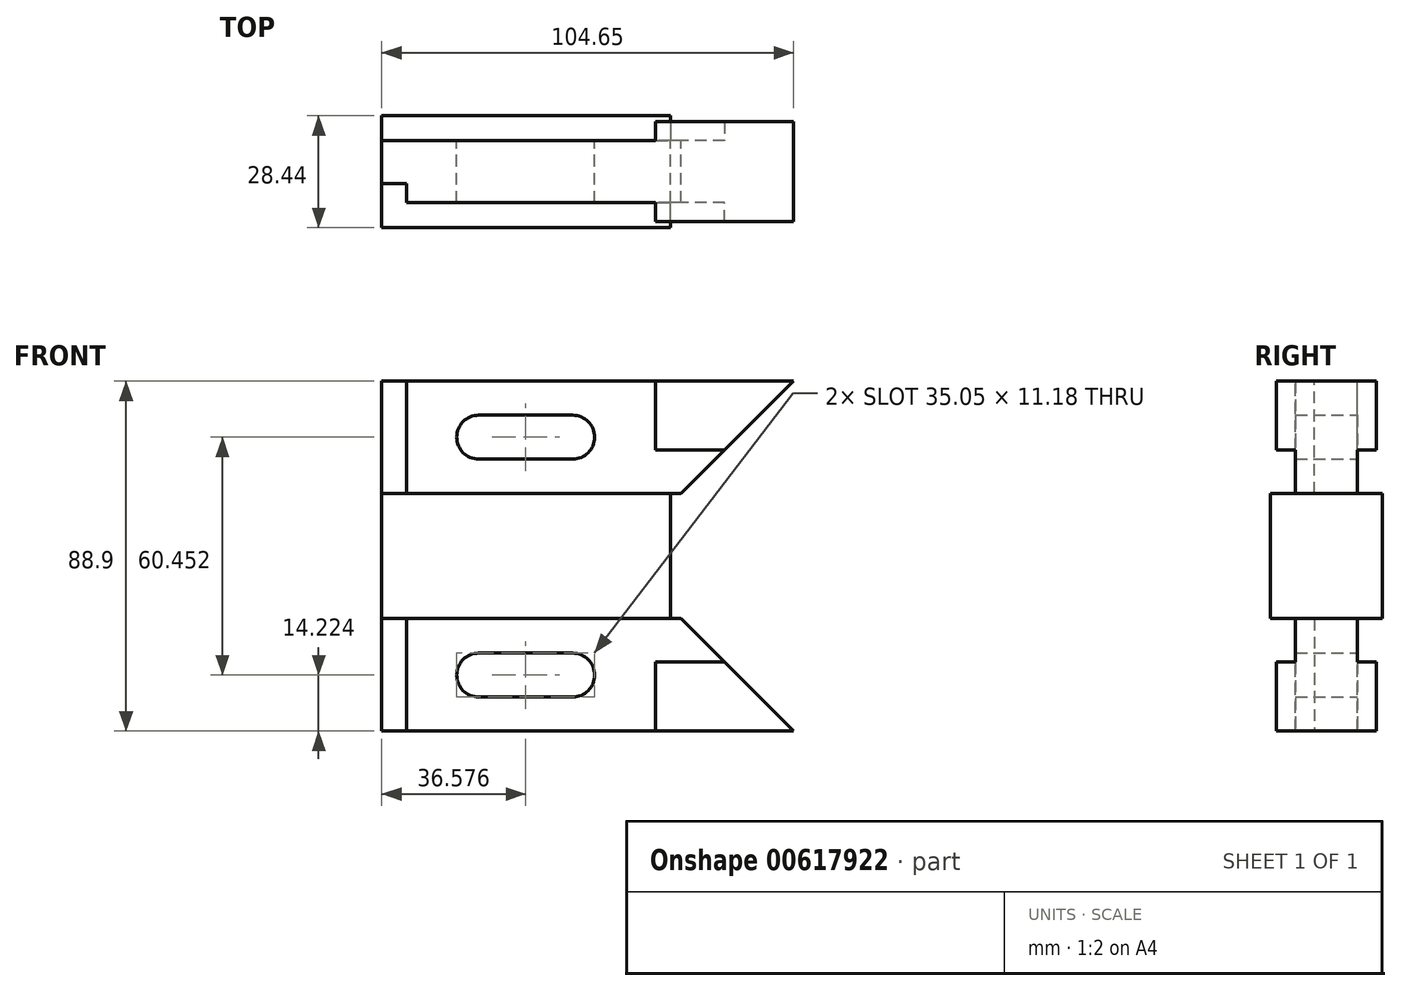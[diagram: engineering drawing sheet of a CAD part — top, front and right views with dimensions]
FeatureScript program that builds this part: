
annotation { "Feature Type Name" : "Feature", "Feature Type Description" : "" }
export const myFeature = defineFeature(function(context is Context, id is Id, definition is map)
    precondition{}
    {
        {
            var Q0;
            Q0=qCreatedBy(makeId("Front.planeOp"),FACE);
            var sketch = newSketch(context, id + "F0", { "sketchPlane" : qUnion([Q0])});
            skLineSegment(sketch, "E0", {"start": v(0, 0) * mm, "end": v(0, 44.45) * mm});
            skLineSegment(sketch, "E1", {"start": v(0, 44.45) * mm, "end": v(104.65, 44.45) * mm});
            skLineSegment(sketch, "E2", {"start": v(104.65, 44.45) * mm, "end": v(76.07, 15.88) * mm});
            skLineSegment(sketch, "E3", {"start": v(76.07, 15.88) * mm, "end": v(0, 15.88) * mm});
            skLineSegment(sketch, "E4", {"start": v(0, 0) * mm, "end": v(94.14, 0) * mm});
            skArc(sketch, "E5", {"start": v(24.64, 35.81) * mm, "mid": v(19.05, 30.23) * mm, "end": v(24.64, 24.64) * mm});
            skArc(sketch, "E6", {"start": v(48.51, 24.64) * mm, "mid": v(54.1, 30.23) * mm, "end": v(48.51, 35.81) * mm});
            skLineSegment(sketch, "E7", {"start": v(24.64, 35.81) * mm, "end": v(48.51, 35.81) * mm});
            skLineSegment(sketch, "E8", {"start": v(24.64, 24.64) * mm, "end": v(48.51, 24.64) * mm});
            skLineSegment(sketch, "E9", {"start": v(69.6, 44.45) * mm, "end": v(69.6, 26.92) * mm});
            skLineSegment(sketch, "E10", {"start": v(69.6, 26.92) * mm, "end": v(87.12, 26.92) * mm});
            skLineSegment(sketch, "E11", {"start": v(6.35, 44.45) * mm, "end": v(6.35, 15.88) * mm});
            skLineSegment(sketch, "E12", {"start": v(24.64, 30.23) * mm, "end": v(48.51, 30.23) * mm, "construction": true});
            skLineSegment(sketch, "E13", {"start": v(-38.06, 0) * mm, "end": v(126.35, 0) * mm, "construction": true});
            skLineSegment(sketch, "E14.MirrorCS", {"start": v(6.35, -44.45) * mm, "end": v(6.35, -15.88) * mm});
            skArc(sketch, "E15.MirrorCS", {"start": v(48.51, -24.64) * mm, "mid": v(54.1, -30.23) * mm, "end": v(48.51, -35.81) * mm});
            skLineSegment(sketch, "E16.MirrorCS", {"start": v(69.6, -26.92) * mm, "end": v(87.12, -26.92) * mm});
            skLineSegment(sketch, "E17.MirrorCS", {"start": v(104.65, -44.45) * mm, "end": v(76.07, -15.88) * mm});
            skArc(sketch, "E18.MirrorCS", {"start": v(24.64, -35.81) * mm, "mid": v(19.05, -30.23) * mm, "end": v(24.64, -24.64) * mm});
            skLineSegment(sketch, "E19.MirrorCS", {"start": v(0, -44.45) * mm, "end": v(104.65, -44.45) * mm});
            skLineSegment(sketch, "E20.MirrorCS", {"start": v(24.64, -24.64) * mm, "end": v(48.51, -24.64) * mm});
            skLineSegment(sketch, "E21.MirrorCS", {"start": v(24.64, -35.81) * mm, "end": v(48.51, -35.81) * mm});
            skLineSegment(sketch, "E22.MirrorCS", {"start": v(24.64, -30.23) * mm, "end": v(48.51, -30.23) * mm, "construction": true});
            skLineSegment(sketch, "E23.MirrorCS", {"start": v(69.6, -44.45) * mm, "end": v(69.6, -26.92) * mm});
            skLineSegment(sketch, "E24.MirrorCS", {"start": v(76.07, -15.88) * mm, "end": v(0, -15.88) * mm});
            skLineSegment(sketch, "E25.MirrorCS", {"start": v(0, 0) * mm, "end": v(0, -44.45) * mm});
            skLineSegment(sketch, "E26", {"start": v(73.4, -15.87) * mm, "end": v(73.4, 15.87) * mm});
            skSolve(sketch);
        }
        {
            var Q0;
            Q0=qSketchRegion(id+"F0",true);
            extrude(context, id + "F1", {"entities" : qUnion([Q0]), "depth" : 7.87 * mm});
        }
        {
            var Q0;
            {var subQ0=sQuery(id+"F0.wireOp",EDGE,"E4");Q0=makeQuery(id+"F0.imprint","IMPRINT",FACE,{"disambiguationData":[TD([[makeQuery(id+"F0.imprint","IMPRINT",EDGE,{"derivedFrom":subQ0}),1.0]])]});}
            var Q1;
            {var subQ1=sQuery(id+"F0.wireOp",EDGE,"E4");Q1=makeQuery(id+"F0.imprint","IMPRINT",FACE,{"disambiguationData":[TD([[makeQuery(id+"F0.imprint","IMPRINT",EDGE,{"derivedFrom":subQ1}),-1.0]])]});}
            extrude(context, id + "F2", {"entities" : qUnion([Q0, Q1]), "operationType" : NewBodyOperationType.ADD, "depth" : 14.22 * mm});
        }
        {
            var Q0;
            {var subQ3=sQuery(id+"F0.wireOp",EDGE,"E9");Q0=makeQuery(id+"F0.imprint","IMPRINT",FACE,{"disambiguationData":[TD([[makeQuery(id+"F0.imprint","IMPRINT",EDGE,{"derivedFrom":subQ3}),1.0]])]});}
            var Q1;
            {var subQ0=sQuery(id+"F0.wireOp",EDGE,"E16.MirrorCS");Q1=makeQuery(id+"F0.imprint","IMPRINT",FACE,{"disambiguationData":[TD([[makeQuery(id+"F0.imprint","IMPRINT",EDGE,{"derivedFrom":subQ0}),-1.0]])]});}
            extrude(context, id + "F3", {"entities" : qUnion([Q0, Q1]), "operationType" : NewBodyOperationType.ADD, "depth" : 12.7 * mm});
        }
        {
            var Q0;
            Q0=makeQuery(id+"F1.opExtrude","SWEPT_BODY",BODY,{"disambiguationData":[OSD([sQuery(id+"F0.wireOp",EDGE,"E0"),sQuery(id+"F0.wireOp",EDGE,"E1"),sQuery(id+"F0.wireOp",EDGE,"E2"),sQuery(id+"F0.wireOp",EDGE,"dfV1hQ6U-fgLX-1oEq-Cl2Z-QLcZu5KokJ9a"),sQuery(id+"F0.wireOp",EDGE,"E5"),sQuery(id+"F0.wireOp",EDGE,"E6"),sQuery(id+"F0.wireOp",EDGE,"E7"),sQuery(id+"F0.wireOp",EDGE,"E8"),sQuery(id+"F0.wireOp",EDGE,"E15.MirrorCS"),sQuery(id+"F0.wireOp",EDGE,"E17.MirrorCS"),sQuery(id+"F0.wireOp",EDGE,"E18.MirrorCS"),sQuery(id+"F0.wireOp",EDGE,"E19.MirrorCS"),sQuery(id+"F0.wireOp",EDGE,"E20.MirrorCS"),sQuery(id+"F0.wireOp",EDGE,"E21.MirrorCS"),sQuery(id+"F0.wireOp",EDGE,"E25.MirrorCS"),sQuery(id+"F0.wireOp",EDGE,"4e4c7bbf-45cc-40e8-b10d-9f1884ca9b700.MirrorCS")])]});
            var Q1;
            Q1=qCreatedBy(makeId("Front.planeOp"),FACE);
            mirror(context, id + "F4", {"operationType" : NewBodyOperationType.ADD, "entities" : qUnion([Q0]), "mirrorPlane" : qUnion([Q1])});
        }
        {
            var Q0;
            {var subQ0=sQuery(id+"F0.wireOp",EDGE,"E8");var subQ1=sQuery(id+"F0.wireOp",EDGE,"E7");var subQ2=sQuery(id+"F0.wireOp",EDGE,"E6");var subQ3=sQuery(id+"F0.wireOp",EDGE,"E25.MirrorCS");var subQ4=sQuery(id+"F0.wireOp",EDGE,"E0");var subQ5=sQuery(id+"F0.wireOp",EDGE,"E5");var subQ6=sQuery(id+"F0.wireOp",EDGE,"E1");var subQ7=sQuery(id+"F0.wireOp",EDGE,"E2");var subQ8=sQuery(id+"F0.wireOp",EDGE,"4e4c7bbf-45cc-40e8-b10d-9f1884ca9b700.MirrorCS");var subQ9=sQuery(id+"F0.wireOp",EDGE,"dfV1hQ6U-fgLX-1oEq-Cl2Z-QLcZu5KokJ9a");Q0=makeQuery(id+"F2.boolean.opBoolean","SPLIT",FACE,{"disambiguationData":[TD([makeQuery(id+"F1.opExtrude","SWEPT_FACE",FACE,{"disambiguationData":[OSD([subQ6])]})])],"derivedFrom":makeQuery(id+"F1.opExtrude","CAP_FACE",FACE,{"disambiguationData":[OSD([subQ4,subQ6,subQ7,subQ9,subQ5,subQ2,subQ1,subQ0,sQuery(id+"F0.wireOp",EDGE,"E15.MirrorCS"),sQuery(id+"F0.wireOp",EDGE,"E17.MirrorCS"),sQuery(id+"F0.wireOp",EDGE,"E18.MirrorCS"),sQuery(id+"F0.wireOp",EDGE,"E19.MirrorCS"),sQuery(id+"F0.wireOp",EDGE,"E20.MirrorCS"),sQuery(id+"F0.wireOp",EDGE,"E21.MirrorCS"),subQ3,subQ8])],"isStart":false})});}
            var sketch = newSketch(context, id + "F5", { "sketchPlane" : qUnion([Q0])});
            skLineSegment(sketch, "E27.0", {"start": v(6.35, 44.45) * mm, "end": v(6.35, 15.88) * mm});
            skLineSegment(sketch, "E28.0", {"start": v(6.35, -44.45) * mm, "end": v(6.35, -15.88) * mm});
            skLineSegment(sketch, "E29", {"start": v(6.35, 44.45) * mm, "end": v(0, 44.45) * mm});
            skLineSegment(sketch, "E30", {"start": v(0, 44.45) * mm, "end": v(0, 15.88) * mm});
            skLineSegment(sketch, "E31", {"start": v(0, 15.88) * mm, "end": v(6.35, 15.88) * mm});
            skLineSegment(sketch, "E32", {"start": v(6.35, -15.88) * mm, "end": v(0, -15.88) * mm});
            skLineSegment(sketch, "E33", {"start": v(0, -15.88) * mm, "end": v(0, -44.45) * mm});
            skLineSegment(sketch, "E34", {"start": v(0, -44.45) * mm, "end": v(6.35, -44.45) * mm});
            skSolve(sketch);
        }
        {
            var Q0;
            Q0=qSketchRegion(id+"F5",true);
            extrude(context, id + "F6", {"entities" : qUnion([Q0]), "operationType" : NewBodyOperationType.REMOVE, "oppositeDirection" : true, "depth" : 4.83 * mm});
        }
    });
